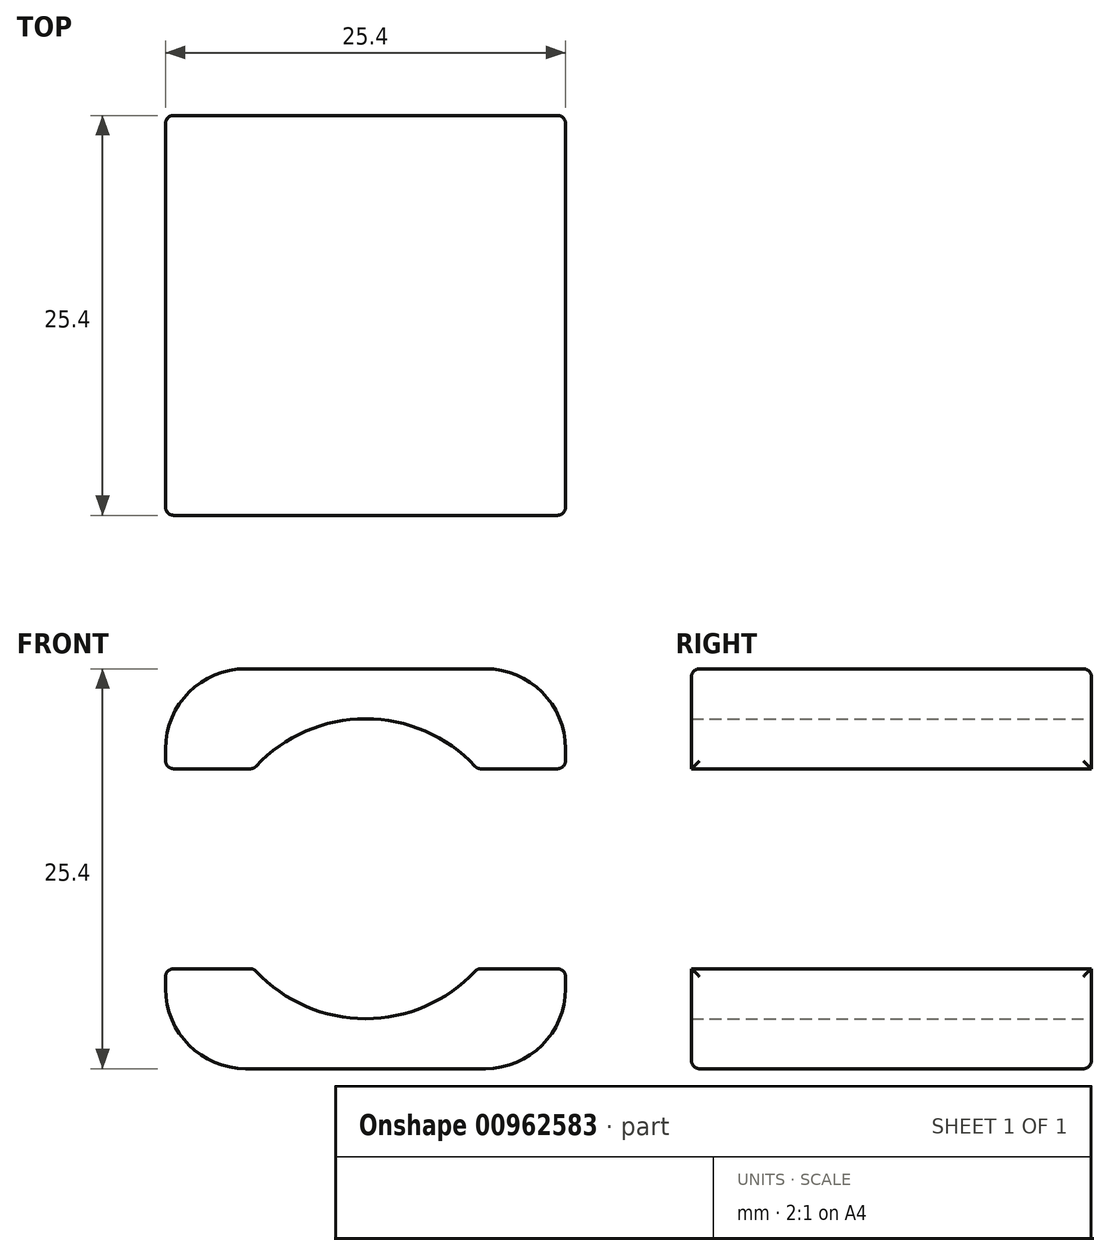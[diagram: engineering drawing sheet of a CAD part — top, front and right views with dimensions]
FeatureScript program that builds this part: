
annotation { "Feature Type Name" : "Feature", "Feature Type Description" : "" }
export const myFeature = defineFeature(function(context is Context, id is Id, definition is map)
    precondition{}
    {
        {
            var Q0;
            Q0=qCreatedBy(makeId("Front.planeOp"),FACE);
            var sketch = newSketch(context, id + "F0", { "sketchPlane" : qUnion([Q0])});
            skLineSegment(sketch, "E0.bottom", {"start": v(12.7, -12.7) * mm, "end": v(-12.7, -12.7) * mm});
            skLineSegment(sketch, "E0.top", {"start": v(12.7, 12.7) * mm, "end": v(-12.7, 12.7) * mm});
            skLineSegment(sketch, "E0.left", {"start": v(12.7, -12.7) * mm, "end": v(12.7, -6.35) * mm});
            skLineSegment(sketch, "E0.right", {"start": v(-12.7, -12.7) * mm, "end": v(-12.7, -6.35) * mm});
            skPoint(sketch, "E0.middle", {"position": v(0, 0) * mm});
            skLineSegment(sketch, "E1.bottom", {"start": v(12.7, -6.35) * mm, "end": v(7.1, -6.35) * mm});
            skLineSegment(sketch, "E1.top", {"start": v(12.7, 6.35) * mm, "end": v(7.1, 6.35) * mm});
            skLineSegment(sketch, "E2.trimOffspring", {"start": v(-12.7, 6.35) * mm, "end": v(-12.7, 12.7) * mm});
            skLineSegment(sketch, "E3.trimOffspring", {"start": v(12.7, 6.35) * mm, "end": v(12.7, 12.7) * mm});
            skArc(sketch, "E4", {"start": v(-7.1, -6.35) * mm, "mid": v(0, -9.53) * mm, "end": v(7.1, -6.35) * mm});
            skArc(sketch, "E5.trimOffspring", {"start": v(7.1, 6.35) * mm, "mid": v(0, 9.53) * mm, "end": v(-7.1, 6.35) * mm});
            skLineSegment(sketch, "E6.trimOffspring", {"start": v(-7.1, 6.35) * mm, "end": v(-12.7, 6.35) * mm});
            skLineSegment(sketch, "E7.trimOffspring", {"start": v(-7.1, -6.35) * mm, "end": v(-12.7, -6.35) * mm});
            skSolve(sketch);
        }
        {
            var Q0;
            Q0=qSketchRegion(id+"F0",true);
            extrude(context, id + "F1", {"entities" : qUnion([Q0]), "endBound" : BoundingType.SYMMETRIC, "depth" : 25.4 * mm, "offsetDistance" : 25.4 * mm});
        }
        {
            var Q0;
            Q0=makeQuery(id+"F1.opExtrude","SWEPT_EDGE",EDGE,{"disambiguationData":[OSD([sQuery(id+"F0.wireOp",EDGE,"E0.top"),sQuery(id+"F0.wireOp",EDGE,"E3.trimOffspring")])]});
            var Q1;
            Q1=makeQuery(id+"F1.opExtrude","SWEPT_EDGE",EDGE,{"disambiguationData":[OSD([sQuery(id+"F0.wireOp",EDGE,"E0.top"),sQuery(id+"F0.wireOp",EDGE,"E2.trimOffspring")])]});
            var Q2;
            Q2=makeQuery(id+"F1.opExtrude","SWEPT_EDGE",EDGE,{"disambiguationData":[OSD([sQuery(id+"F0.wireOp",EDGE,"E0.bottom"),sQuery(id+"F0.wireOp",EDGE,"E0.left")])]});
            var Q3;
            Q3=makeQuery(id+"F1.opExtrude","SWEPT_EDGE",EDGE,{"disambiguationData":[OSD([sQuery(id+"F0.wireOp",EDGE,"E0.bottom"),sQuery(id+"F0.wireOp",EDGE,"E0.right")])]});
            fillet(context, id + "F2", {"entities" : qUnion([Q0, Q1, Q2, Q3]), "radius" : 5.08 * mm, "tangentPropagation" : true, "allowEdgeOverflow" : false});
        }
        {
            var Q0;
            Q0=makeQuery(id+"F1.opExtrude","CAP_EDGE",EDGE,{"disambiguationData":[OSD([sQuery(id+"F0.wireOp",EDGE,"E0.top")])],"isStart":false});
            var Q1;
            Q1=makeQuery(id+"F1.opExtrude","CAP_EDGE",EDGE,{"disambiguationData":[OSD([sQuery(id+"F0.wireOp",EDGE,"E0.top")])],"isStart":true});
            var Q2;
            Q2=makeQuery(id+"F1.opExtrude","CAP_EDGE",EDGE,{"disambiguationData":[OSD([sQuery(id+"F0.wireOp",EDGE,"E0.bottom")])],"isStart":false});
            var Q3;
            Q3=makeQuery(id+"F1.opExtrude","CAP_EDGE",EDGE,{"disambiguationData":[OSD([sQuery(id+"F0.wireOp",EDGE,"E0.bottom")])],"isStart":true});
            var Q4;
            Q4=makeQuery(id+"F1.opExtrude","SWEPT_EDGE",EDGE,{"disambiguationData":[OSD([sQuery(id+"F0.wireOp",EDGE,"E2.trimOffspring"),sQuery(id+"F0.wireOp",EDGE,"E6.trimOffspring")])]});
            var Q5;
            Q5=makeQuery(id+"F1.opExtrude","SWEPT_EDGE",EDGE,{"disambiguationData":[OSD([sQuery(id+"F0.wireOp",EDGE,"E5.trimOffspring"),sQuery(id+"F0.wireOp",EDGE,"E6.trimOffspring")])]});
            var Q6;
            Q6=makeQuery(id+"F1.opExtrude","SWEPT_EDGE",EDGE,{"disambiguationData":[OSD([sQuery(id+"F0.wireOp",EDGE,"E1.top"),sQuery(id+"F0.wireOp",EDGE,"E5.trimOffspring")])]});
            var Q7;
            Q7=makeQuery(id+"F1.opExtrude","SWEPT_EDGE",EDGE,{"disambiguationData":[OSD([sQuery(id+"F0.wireOp",EDGE,"E1.top"),sQuery(id+"F0.wireOp",EDGE,"E3.trimOffspring")])]});
            var Q8;
            Q8=makeQuery(id+"F1.opExtrude","SWEPT_EDGE",EDGE,{"disambiguationData":[OSD([sQuery(id+"F0.wireOp",EDGE,"E0.left"),sQuery(id+"F0.wireOp",EDGE,"E1.bottom")])]});
            var Q9;
            Q9=makeQuery(id+"F1.opExtrude","SWEPT_EDGE",EDGE,{"disambiguationData":[OSD([sQuery(id+"F0.wireOp",EDGE,"E0.right"),sQuery(id+"F0.wireOp",EDGE,"E7.trimOffspring")])]});
            var Q10;
            Q10=makeQuery(id+"F1.opExtrude","SWEPT_EDGE",EDGE,{"disambiguationData":[OSD([sQuery(id+"F0.wireOp",EDGE,"E1.bottom"),sQuery(id+"F0.wireOp",EDGE,"E4")])]});
            var Q11;
            Q11=makeQuery(id+"F1.opExtrude","SWEPT_EDGE",EDGE,{"disambiguationData":[OSD([sQuery(id+"F0.wireOp",EDGE,"E4"),sQuery(id+"F0.wireOp",EDGE,"E7.trimOffspring")])]});
            fillet(context, id + "F3", {"entities" : qUnion([Q0, Q1, Q2, Q3, Q4, Q5, Q6, Q7, Q8, Q9, Q10, Q11]), "radius" : 0.5 * mm, "tangentPropagation" : true, "defaultsChanged" : false, "vertexSettings" : [], "allowEdgeOverflow" : false});
        }
    });
